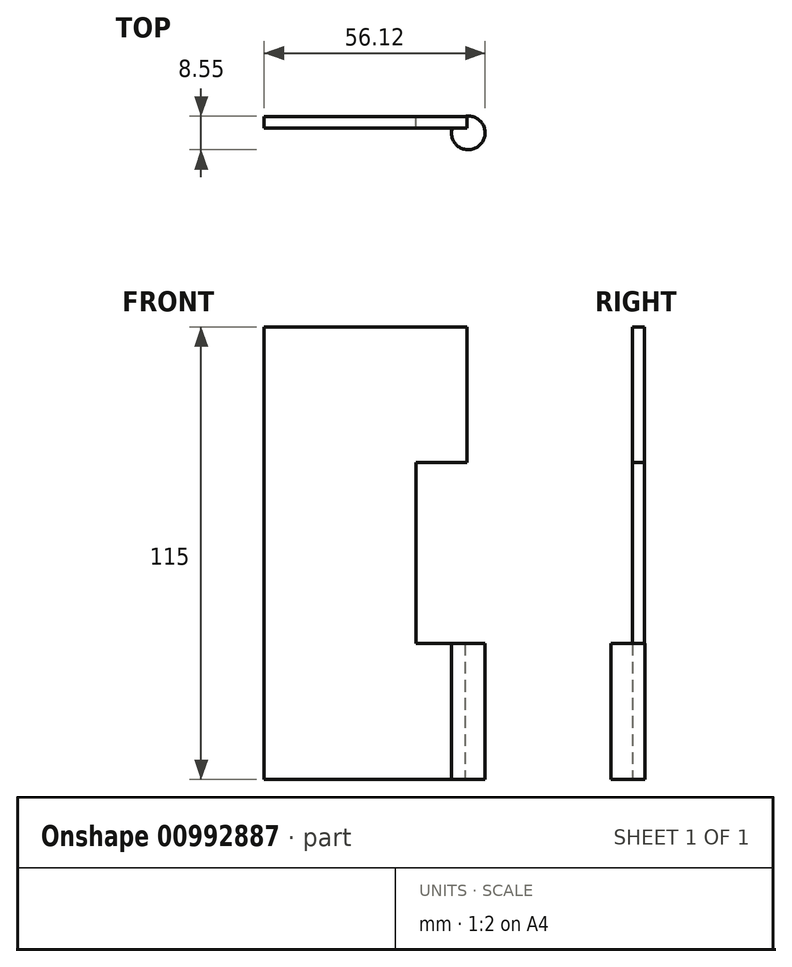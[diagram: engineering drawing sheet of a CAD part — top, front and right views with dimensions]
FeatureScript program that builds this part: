
annotation { "Feature Type Name" : "Feature", "Feature Type Description" : "" }
export const myFeature = defineFeature(function(context is Context, id is Id, definition is map)
    precondition{}
    {
        {
            var Q0;
            Q0=qCreatedBy(makeId("Front.planeOp"),FACE);
            var sketch = newSketch(context, id + "F0", { "sketchPlane" : qUnion([Q0])});
            skLineSegment(sketch, "E0", {"start": v(0, 0) * mm, "end": v(0, 115) * mm});
            skLineSegment(sketch, "E1", {"start": v(0, 115) * mm, "end": v(51.5, 115) * mm});
            skLineSegment(sketch, "E2", {"start": v(51.5, 115) * mm, "end": v(51.5, 80.5) * mm});
            skLineSegment(sketch, "E3", {"start": v(51.5, 80.5) * mm, "end": v(38.5, 80.5) * mm});
            skLineSegment(sketch, "E4", {"start": v(38.5, 80.5) * mm, "end": v(38.5, 34.5) * mm});
            skLineSegment(sketch, "E5", {"start": v(38.5, 34.5) * mm, "end": v(51.5, 34.5) * mm});
            skLineSegment(sketch, "E6", {"start": v(51.5, 34.5) * mm, "end": v(51.5, 0) * mm});
            skLineSegment(sketch, "E7", {"start": v(51.5, 0) * mm, "end": v(0, 0) * mm});
            skSolve(sketch);
        }
        {
            var Q0;
            Q0=makeQuery(id+"F0.imprint","IMPRINT",FACE,{"disambiguationData":[TD([[makeQuery(id+"F0.imprint","IMPRINT",EDGE,{"derivedFrom":sQuery(id+"F0.wireOp",EDGE,"E0")}),-1.0]])]});
            extrude(context, id + "F1", {"entities" : qUnion([Q0]), "depth" : 3 * mm, "offsetDistance" : 25 * mm});
        }
        {
            var Q0;
            Q0=qCreatedBy(makeId("Top.planeOp"),FACE);
            var sketch = newSketch(context, id + "F2", { "sketchPlane" : qUnion([Q0])});
            skCircle(sketch, "E8", {"center": v(51.84, -4.2) * mm, "radius": 4.28 * mm});
            skPoint(sketch, "E8.first.point", {"position": v(51.01, 0) * mm});
            skPoint(sketch, "E8.second.point", {"position": v(53.87, -7.96) * mm});
            skPoint(sketch, "E8.third.point", {"position": v(49.8, -7.96) * mm});
            skSolve(sketch);
        }
        {
            var Q0;
            Q0=makeQuery(id+"F2.imprint","IMPRINT",FACE,{"disambiguationData":[TD([[makeQuery(id+"F2.imprint","IMPRINT",EDGE,{"derivedFrom":sQuery(id+"F2.wireOp",EDGE,"E8")}),1.0]])]});
            extrude(context, id + "F3", {"entities" : qUnion([Q0]), "operationType" : NewBodyOperationType.ADD, "depth" : 34.5 * mm, "offsetDistance" : 25 * mm});
        }
    });
